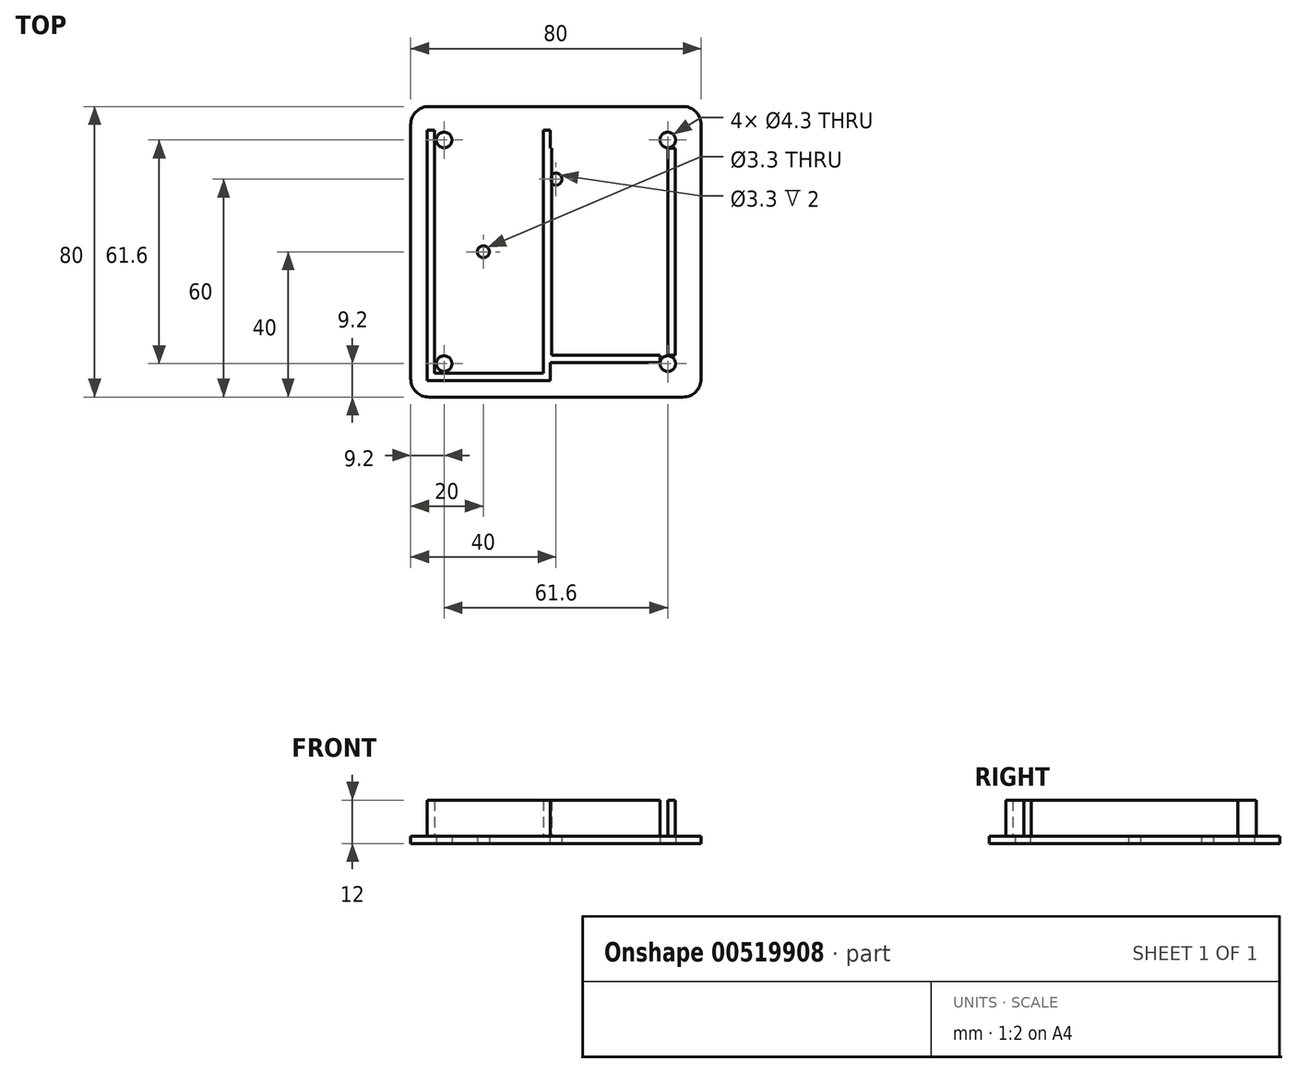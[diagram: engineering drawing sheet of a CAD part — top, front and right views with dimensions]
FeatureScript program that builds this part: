
annotation { "Feature Type Name" : "Feature", "Feature Type Description" : "" }
export const myFeature = defineFeature(function(context is Context, id is Id, definition is map)
    precondition{}
    {
        {
            var Q0;
            Q0=qCreatedBy(makeId("Top.planeOp"),FACE);
            var sketch = newSketch(context, id + "F0", { "sketchPlane" : qUnion([Q0])});
            skLineSegment(sketch, "E0", {"start": v(0, 0) * mm, "end": v(40, 0) * mm, "construction": true});
            skLineSegment(sketch, "E1", {"start": v(40, 0) * mm, "end": v(40, -40) * mm, "construction": true});
            skLineSegment(sketch, "E2", {"start": v(35, -40) * mm, "end": v(-35, -40) * mm});
            skLineSegment(sketch, "E3", {"start": v(-40, -35) * mm, "end": v(-40, 35) * mm});
            skLineSegment(sketch, "E4", {"start": v(-35, 40) * mm, "end": v(35, 40) * mm});
            skLineSegment(sketch, "E5", {"start": v(40, 35) * mm, "end": v(40, -35) * mm});
            skLineSegment(sketch, "E6", {"start": v(40, -40) * mm, "end": v(30.8, -40) * mm, "construction": true});
            skLineSegment(sketch, "E7", {"start": v(30.8, -40) * mm, "end": v(30.8, -30.8) * mm, "construction": true});
            skCircle(sketch, "E8", {"center": v(30.8, -30.8) * mm, "radius": 2.15 * mm});
            skLineSegment(sketch, "E9", {"start": v(30.8, -30.8) * mm, "end": v(37.3, -30.8) * mm, "construction": true});
            skLineSegment(sketch, "E10", {"start": v(37.3, -30.8) * mm, "end": v(37.3, -32.4) * mm, "construction": true});
            skLineSegment(sketch, "E11", {"start": v(30.8, -30.8) * mm, "end": v(30.8, -35.8) * mm, "construction": true});
            skLineSegment(sketch, "E12", {"start": v(30.8, -35.8) * mm, "end": v(32.1, -35.8) * mm, "construction": true});
            skLineSegment(sketch, "E13.MirrorCS", {"start": v(30.8, 30.8) * mm, "end": v(30.8, 35.8) * mm, "construction": true});
            skLineSegment(sketch, "E14.MirrorCS", {"start": v(30.8, 30.8) * mm, "end": v(37.3, 30.8) * mm, "construction": true});
            skCircle(sketch, "E15.MirrorC", {"center": v(30.8, 30.8) * mm, "radius": 2.15 * mm});
            skCircle(sketch, "E16.MirrorC", {"center": v(-30.8, 30.8) * mm, "radius": 2.15 * mm});
            skCircle(sketch, "E17.MirrorC", {"center": v(-30.8, -30.8) * mm, "radius": 2.15 * mm});
            skPoint(sketch, "E18.visualSharp", {"position": v(-40, 40) * mm});
            skArc(sketch, "E18.filletArc", {"start": v(-35, 40) * mm, "mid": v(-38.54, 38.54) * mm, "end": v(-40, 35) * mm});
            skPoint(sketch, "E19.visualSharp", {"position": v(40, 40) * mm});
            skArc(sketch, "E19.filletArc", {"start": v(40, 35) * mm, "mid": v(38.54, 38.54) * mm, "end": v(35, 40) * mm});
            skPoint(sketch, "E20.visualSharp", {"position": v(40, -40) * mm});
            skArc(sketch, "E20.filletArc", {"start": v(35, -40) * mm, "mid": v(38.54, -38.54) * mm, "end": v(40, -35) * mm});
            skPoint(sketch, "E21.visualSharp", {"position": v(-40, -40) * mm});
            skArc(sketch, "E21.filletArc", {"start": v(-40, -35) * mm, "mid": v(-38.54, -38.54) * mm, "end": v(-35, -40) * mm});
            skLineSegment(sketch, "E22", {"start": v(30.8, 30.8) * mm, "end": v(30.8, -30.8) * mm, "construction": true});
            skLineSegment(sketch, "E23", {"start": v(-30.8, 30.8) * mm, "end": v(30.8, 30.8) * mm, "construction": true});
            skLineSegment(sketch, "E24", {"start": v(40, 0) * mm, "end": v(20, 0) * mm, "construction": true});
            skCircle(sketch, "E25", {"center": v(20, 0) * mm, "radius": 1.65 * mm});
            skCircle(sketch, "E26.MirrorC", {"center": v(-20, 0) * mm, "radius": 1.65 * mm});
            skLineSegment(sketch, "E27", {"start": v(0, -40) * mm, "end": v(0, -20) * mm, "construction": true});
            skCircle(sketch, "E28", {"center": v(0, -20) * mm, "radius": 1.65 * mm});
            skCircle(sketch, "E29.MirrorC", {"center": v(0, 20) * mm, "radius": 1.65 * mm});
            skSolve(sketch);
        }
        {
            var Q0;
            Q0=makeQuery(id+"F0.imprint","IMPRINT",FACE,{"disambiguationData":[TD([[makeQuery(id+"F0.imprint","IMPRINT",EDGE,{"derivedFrom":sQuery(id+"F0.wireOp",EDGE,"E26.MirrorC")}),-1.0]])]});
            var Q1;
            Q1=makeQuery(id+"F0.imprint","IMPRINT",FACE,{"disambiguationData":[TD([[makeQuery(id+"F0.imprint","IMPRINT",EDGE,{"derivedFrom":sQuery(id+"F0.wireOp",EDGE,"E28")}),1.0]])]});
            var Q2;
            Q2=makeQuery(id+"F0.imprint","IMPRINT",FACE,{"disambiguationData":[TD([[makeQuery(id+"F0.imprint","IMPRINT",EDGE,{"derivedFrom":sQuery(id+"F0.wireOp",EDGE,"E2")}),-1.0]])]});
            var Q3;
            Q3=makeQuery(id+"F0.imprint","IMPRINT",FACE,{"disambiguationData":[TD([[makeQuery(id+"F0.imprint","IMPRINT",EDGE,{"derivedFrom":sQuery(id+"F0.wireOp",EDGE,"E25")}),1.0]])]});
            var Q4;
            Q4=makeQuery(id+"F0.imprint","IMPRINT",FACE,{"disambiguationData":[TD([[makeQuery(id+"F0.imprint","IMPRINT",EDGE,{"derivedFrom":sQuery(id+"F0.wireOp",EDGE,"E29.MirrorC")}),-1.0]])]});
            extrude(context, id + "F1", {"entities" : qUnion([Q0, Q1, Q2, Q3, Q4]), "depth" : 2 * mm, "offsetDistance" : 25 * mm});
        }
        {
            var Q0;
            Q0=makeQuery(id+"F1.opExtrude","CAP_FACE",FACE,{"disambiguationData":[OSD([sQuery(id+"F0.wireOp",EDGE,"E2"),sQuery(id+"F0.wireOp",EDGE,"E3"),sQuery(id+"F0.wireOp",EDGE,"E4"),sQuery(id+"F0.wireOp",EDGE,"E5"),sQuery(id+"F0.wireOp",EDGE,"E8"),sQuery(id+"F0.wireOp",EDGE,"E15.MirrorC"),sQuery(id+"F0.wireOp",EDGE,"E16.MirrorC"),sQuery(id+"F0.wireOp",EDGE,"E17.MirrorC"),sQuery(id+"F0.wireOp",EDGE,"E18.filletArc"),sQuery(id+"F0.wireOp",EDGE,"E19.filletArc"),sQuery(id+"F0.wireOp",EDGE,"E20.filletArc"),sQuery(id+"F0.wireOp",EDGE,"E21.filletArc"),sQuery(id+"F0.wireOp",EDGE,"E25"),sQuery(id+"F0.wireOp",EDGE,"E26.MirrorC"),sQuery(id+"F0.wireOp",EDGE,"E28"),sQuery(id+"F0.wireOp",EDGE,"E29.MirrorC")])],"isStart":false});
            var sketch = newSketch(context, id + "F2", { "sketchPlane" : qUnion([Q0])});
            skLineSegment(sketch, "E30.0", {"start": v(-40, -35) * mm, "end": v(-40, 35) * mm});
            skLineSegment(sketch, "E31.0", {"start": v(-35, 40) * mm, "end": v(35, 40) * mm});
            skLineSegment(sketch, "E32.0", {"start": v(40, 35) * mm, "end": v(40, -35) * mm});
            skLineSegment(sketch, "E33.0", {"start": v(35, -40) * mm, "end": v(-35, -40) * mm});
            skLineSegment(sketch, "E34.bottom", {"start": v(90.11, 32.8) * mm, "end": v(122.11, 32.8) * mm, "construction": true});
            skLineSegment(sketch, "E34.top", {"start": v(90.11, -24.2) * mm, "end": v(122.11, -24.2) * mm, "construction": true});
            skLineSegment(sketch, "E34.left", {"start": v(90.11, 32.8) * mm, "end": v(90.11, -24.2) * mm, "construction": true});
            skLineSegment(sketch, "E34.right", {"start": v(122.11, 32.8) * mm, "end": v(122.11, -24.2) * mm, "construction": true});
            skPoint(sketch, "E35.0", {"position": v(-30.8, 30.8) * mm});
            skPoint(sketch, "E35.1", {"position": v(-30.8, -30.8) * mm});
            skCircle(sketch, "E36", {"center": v(-30.8, 30.8) * mm, "radius": 2.7 * mm, "construction": true});
            skCircle(sketch, "E37", {"center": v(-30.8, -30.8) * mm, "radius": 2.7 * mm, "construction": true});
            skLineSegment(sketch, "E38", {"start": v(-30.8, 33.5) * mm, "end": v(-30.8, -33.5) * mm, "construction": true});
            skLineSegment(sketch, "E39", {"start": v(-30.8, 33.5) * mm, "end": v(-33.5, 33.5) * mm, "construction": true});
            skLineSegment(sketch, "E40.bottom", {"start": v(-33.5, 33.5) * mm, "end": v(-3.5, 33.5) * mm, "construction": true});
            skLineSegment(sketch, "E40.top", {"start": v(-33.5, -33.5) * mm, "end": v(-3.5, -33.5) * mm, "construction": true});
            skLineSegment(sketch, "E40.left", {"start": v(-33.5, 33.5) * mm, "end": v(-33.5, -33.5) * mm, "construction": true});
            skLineSegment(sketch, "E40.right", {"start": v(-3.5, 33.5) * mm, "end": v(-3.5, -33.5) * mm, "construction": true});
            skLineSegment(sketch, "E41.bottom", {"start": v(-33.5, 33.5) * mm, "end": v(-35.5, 33.5) * mm});
            skLineSegment(sketch, "E41.top", {"start": v(-33.5, -33.5) * mm, "end": v(-35.5, -33.5) * mm});
            skLineSegment(sketch, "E41.left", {"start": v(-33.5, 33.5) * mm, "end": v(-33.5, -33.5) * mm});
            skLineSegment(sketch, "E41.right", {"start": v(-35.5, 33.5) * mm, "end": v(-35.5, -33.5) * mm});
            skLineSegment(sketch, "E42.bottom", {"start": v(-35.5, -33.5) * mm, "end": v(-3.5, -33.5) * mm});
            skLineSegment(sketch, "E42.top", {"start": v(-35.5, -35.5) * mm, "end": v(-3.5, -35.5) * mm});
            skLineSegment(sketch, "E42.left", {"start": v(-35.5, -33.5) * mm, "end": v(-35.5, -35.5) * mm});
            skLineSegment(sketch, "E42.right", {"start": v(-3.5, -33.5) * mm, "end": v(-3.5, -35.5) * mm});
            skLineSegment(sketch, "E43.bottom", {"start": v(-3.5, -35.5) * mm, "end": v(-1.5, -35.5) * mm});
            skLineSegment(sketch, "E43.top", {"start": v(-3.5, 33.5) * mm, "end": v(-1.5, 33.5) * mm});
            skLineSegment(sketch, "E43.left", {"start": v(-3.5, -35.5) * mm, "end": v(-3.5, 33.5) * mm});
            skLineSegment(sketch, "E43.right", {"start": v(-1.5, -35.5) * mm, "end": v(-1.5, 33.5) * mm});
            skCircle(sketch, "E44.0", {"center": v(30.8, 30.8) * mm, "radius": 2.15 * mm, "construction": true});
            skArc(sketch, "E45.0", {"start": v(30.8, -28.65) * mm, "mid": v(29.28, -29.28) * mm, "end": v(28.65, -30.8) * mm});
            skLineSegment(sketch, "E46", {"start": v(30.8, 28.65) * mm, "end": v(30.8, -28.65) * mm, "construction": true});
            skLineSegment(sketch, "E47", {"start": v(30.8, -28.65) * mm, "end": v(30.8, -28.5) * mm});
            skLineSegment(sketch, "E48.bottom", {"start": v(30.8, -28.5) * mm, "end": v(-1.2, -28.5) * mm});
            skLineSegment(sketch, "E48.top", {"start": v(30.8, 28.5) * mm, "end": v(-1.2, 28.5) * mm, "construction": true});
            skLineSegment(sketch, "E48.left", {"start": v(30.8, -28.5) * mm, "end": v(30.8, 28.5) * mm});
            skLineSegment(sketch, "E48.right", {"start": v(-1.2, -28.5) * mm, "end": v(-1.2, 28.5) * mm});
            skLineSegment(sketch, "E49", {"start": v(-1.2, 28.5) * mm, "end": v(-1.5, 28.5) * mm});
            skLineSegment(sketch, "E50", {"start": v(-1.2, -28.5) * mm, "end": v(-1.5, -28.5) * mm});
            skLineSegment(sketch, "E51", {"start": v(28.65, -30.5) * mm, "end": v(28.65, -28.5) * mm, "construction": true});
            skLineSegment(sketch, "E52.bottom", {"start": v(-1.5, -28.5) * mm, "end": v(28.65, -28.5) * mm});
            skLineSegment(sketch, "E52.top", {"start": v(-1.5, -30.5) * mm, "end": v(28.65, -30.5) * mm});
            skLineSegment(sketch, "E52.left", {"start": v(-1.5, -28.5) * mm, "end": v(-1.5, -30.5) * mm});
            skLineSegment(sketch, "E52.right", {"start": v(28.65, -28.5) * mm, "end": v(28.65, -30.5) * mm});
            skLineSegment(sketch, "E53.bottom", {"start": v(30.8, 28.5) * mm, "end": v(32.8, 28.5) * mm});
            skLineSegment(sketch, "E53.top", {"start": v(30.8, -28.5) * mm, "end": v(32.8, -28.5) * mm});
            skLineSegment(sketch, "E53.left", {"start": v(30.8, 28.5) * mm, "end": v(30.8, -28.5) * mm});
            skLineSegment(sketch, "E53.right", {"start": v(32.8, 28.5) * mm, "end": v(32.8, -28.5) * mm});
            skLineSegment(sketch, "E54", {"start": v(28.65, -28.5) * mm, "end": v(30.8, -28.5) * mm});
            skSolve(sketch);
        }
        {
            var Q0;
            Q0 = qSketchRegion(id + "F2", true);
            extrude(context, id + "F3", {"entities" : qUnion([Q0]), "operationType" : NewBodyOperationType.ADD, "depth" : 10 * mm, "offsetDistance" : 25 * mm});
        }
    });
